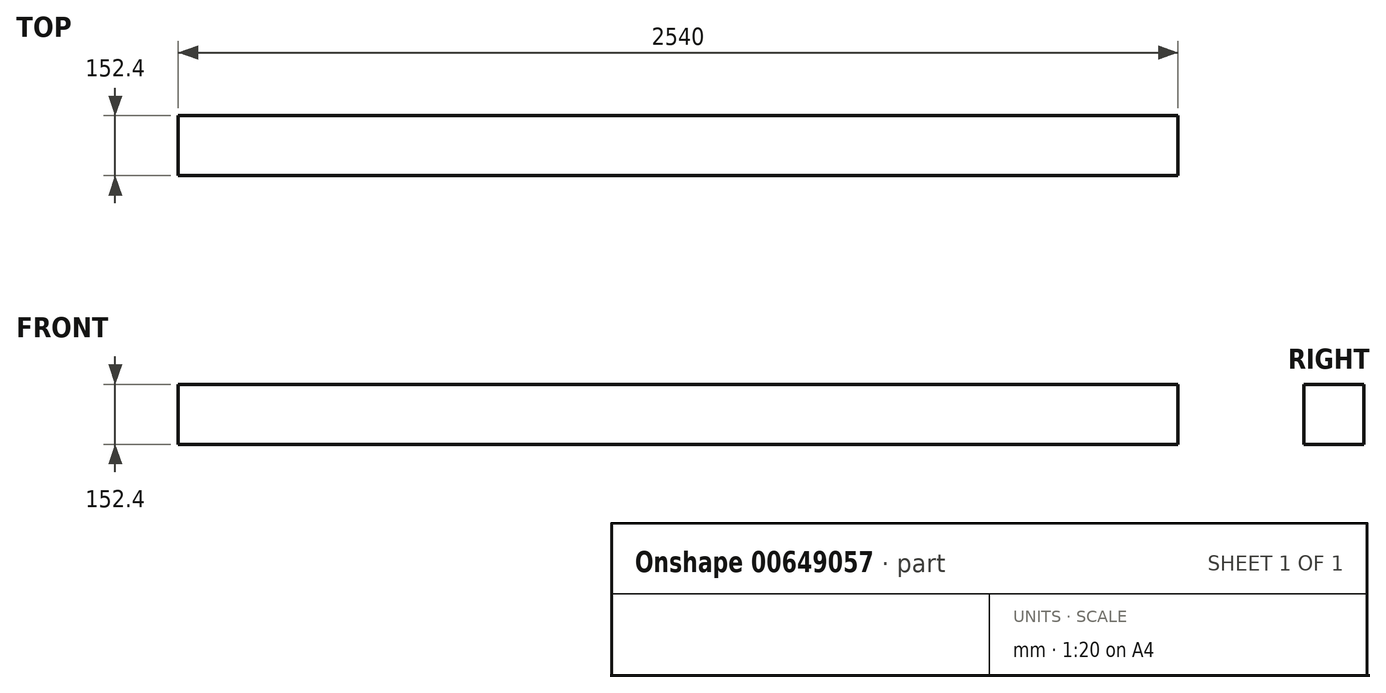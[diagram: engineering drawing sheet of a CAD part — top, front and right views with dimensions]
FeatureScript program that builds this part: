
annotation { "Feature Type Name" : "Feature", "Feature Type Description" : "" }
export const myFeature = defineFeature(function(context is Context, id is Id, definition is map)
    precondition{}
    {
        {
            var Q0;
            Q0=qCreatedBy(makeId("Top.planeOp"),FACE);
            var sketch = newSketch(context, id + "F0", { "sketchPlane" : qUnion([Q0])});
            skLineSegment(sketch, "E0.bottom", {"start": v(-1266.34, 173.24) * mm, "end": v(1273.66, 173.24) * mm});
            skLineSegment(sketch, "E0.top", {"start": v(-1266.34, 20.84) * mm, "end": v(1273.66, 20.84) * mm});
            skLineSegment(sketch, "E0.left", {"start": v(-1266.34, 173.24) * mm, "end": v(-1266.34, 20.84) * mm});
            skLineSegment(sketch, "E0.right", {"start": v(1273.66, 173.24) * mm, "end": v(1273.66, 20.84) * mm});
            skSolve(sketch);
        }
        {
            var Q0;
            Q0 = qSketchRegion(id + "F0", true);
            extrude(context, id + "F1", {"entities" : qUnion([Q0]), "depth" : 152.4 * mm, "offsetDistance" : 25.4 * mm});
        }
    });
